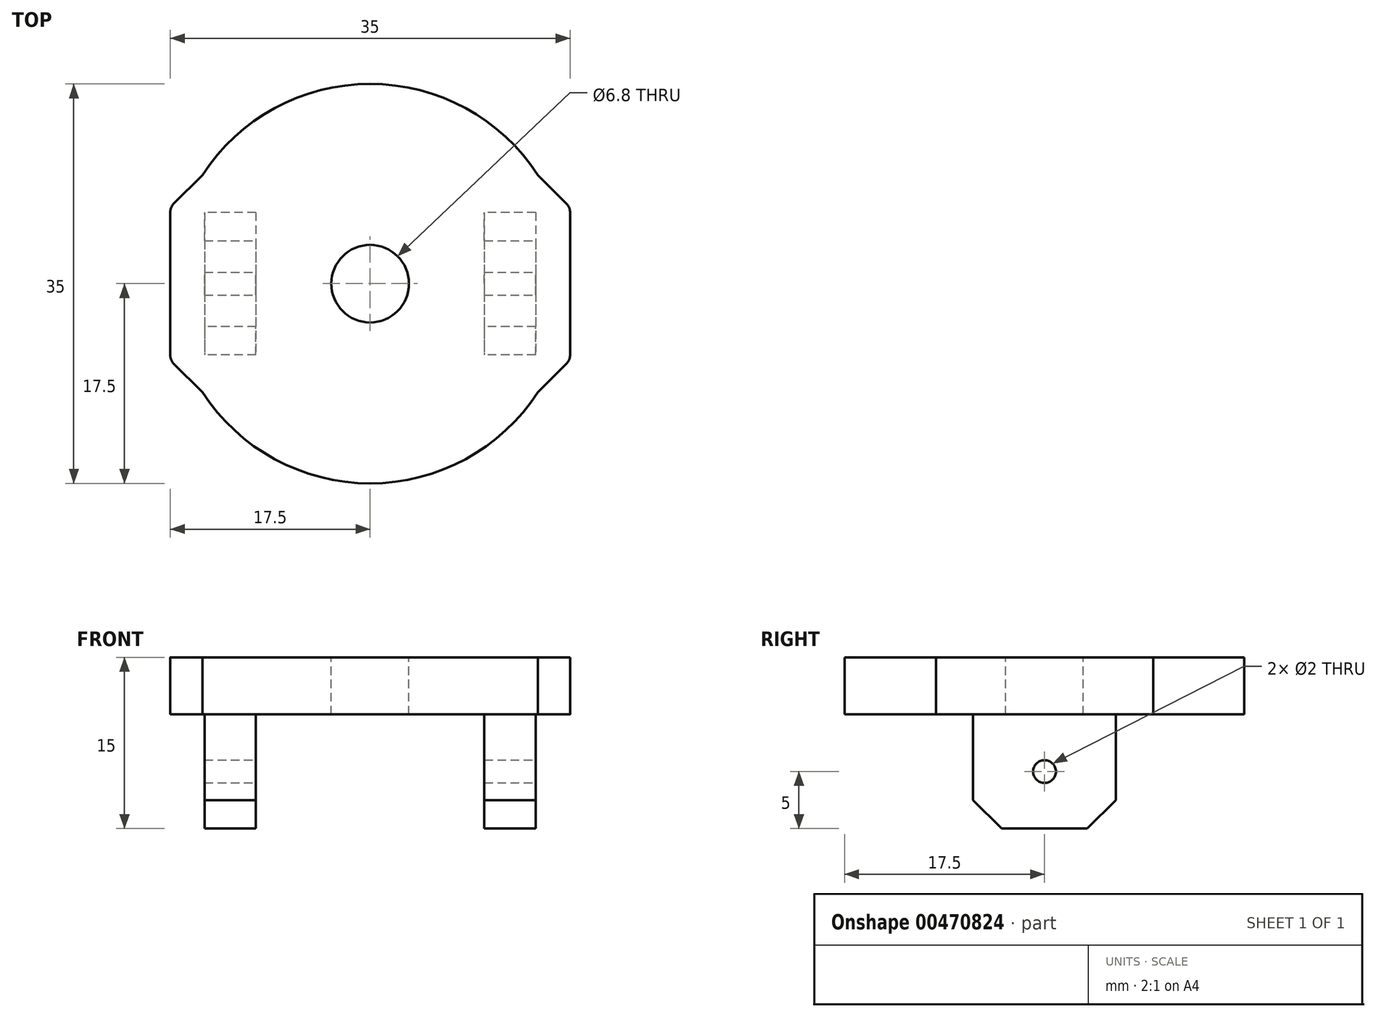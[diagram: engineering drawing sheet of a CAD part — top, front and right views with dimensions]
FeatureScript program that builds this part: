
annotation { "Feature Type Name" : "Feature", "Feature Type Description" : "" }
export const myFeature = defineFeature(function(context is Context, id is Id, definition is map)
    precondition{}
    {
        {
            var Q0;
            Q0=qCreatedBy(makeId("Top.planeOp"),FACE);
            var sketch = newSketch(context, id + "F0", { "sketchPlane" : qUnion([Q0])});
            skLineSegment(sketch, "E0.left", {"start": v(25, -7.7) * mm, "end": v(25, 7.7) * mm});
            skLineSegment(sketch, "E0.right", {"start": v(-25, -7.7) * mm, "end": v(-25, 7.7) * mm});
            skPoint(sketch, "E0.middle", {"position": v(0, 0) * mm});
            skEllipticalArc(sketch, "E1", {});
            skPoint(sketch, "E2.visualSharp", {"position": v(-25, 12.78) * mm});
            skArc(sketch, "E2.filletArc", {"start": v(-19.86, 15.83) * mm, "mid": v(-23.6, 12.5) * mm, "end": v(-25, 7.7) * mm});
            skArc(sketch, "E3.filletArc", {"start": v(-25, -7.7) * mm, "mid": v(-23.6, -12.5) * mm, "end": v(-19.86, -15.83) * mm});
            skEllipticalArc(sketch, "E4.trimOffspring", {});
            skPoint(sketch, "E5.visualSharp", {"position": v(25, 12.78) * mm});
            skArc(sketch, "E5.filletArc", {"start": v(25, 7.7) * mm, "mid": v(23.6, 12.5) * mm, "end": v(19.86, 15.83) * mm});
            skPoint(sketch, "E6.visualSharp", {"position": v(25, -12.78) * mm});
            skArc(sketch, "E6.filletArc", {"start": v(19.86, -15.83) * mm, "mid": v(23.6, -12.5) * mm, "end": v(25, -7.7) * mm});
            const initialGuessF0  = {"E1": [0, 0, 1, 0, 0.0325, 0.02, 4.054867696901255, 5.3699102638681255], "E4.trimOffspring": [0, 0, 1, 0, 0.0325, 0.02, 0.913275043311461, 2.2283176102783337]};
            skSetInitialGuess(sketch, initialGuessF0);
            skSolve(sketch);
        }
        {
            var Q0;
            Q0=makeQuery(id+"F0.imprint","IMPRINT",FACE,{"disambiguationData":[TD([[makeQuery(id+"F0.imprint","IMPRINT",EDGE,{"derivedFrom":sQuery(id+"F0.wireOp",EDGE,"E0.left")}),1.0]])]});
            extrude(context, id + "F1", {"entities" : qUnion([Q0]), "depth" : 5 * mm});
        }
        {
            var Q0;
            Q0=makeQuery(id+"F1.opExtrude","CAP_FACE",FACE,{"disambiguationData":[OSD([sQuery(id+"F0.wireOp",EDGE,"E0.left"),sQuery(id+"F0.wireOp",EDGE,"E0.right"),sQuery(id+"F0.wireOp",EDGE,"E1"),sQuery(id+"F0.wireOp",EDGE,"E2.filletArc"),sQuery(id+"F0.wireOp",EDGE,"E3.filletArc"),sQuery(id+"F0.wireOp",EDGE,"E4.trimOffspring"),sQuery(id+"F0.wireOp",EDGE,"E5.filletArc"),sQuery(id+"F0.wireOp",EDGE,"E6.filletArc")])],"isStart":true});
            var sketch = newSketch(context, id + "F2", { "sketchPlane" : qUnion([Q0])});
            skLineSegment(sketch, "E7.bottom", {"start": v(14.5, -6.25) * mm, "end": v(10, -6.25) * mm});
            skLineSegment(sketch, "E7.top", {"start": v(14.5, 6.25) * mm, "end": v(10, 6.25) * mm});
            skLineSegment(sketch, "E7.left", {"start": v(14.5, -6.25) * mm, "end": v(14.5, 6.25) * mm});
            skLineSegment(sketch, "E7.right", {"start": v(-14.5, -6.25) * mm, "end": v(-14.5, 6.25) * mm});
            skPoint(sketch, "E7.middle", {"position": v(0, 0) * mm});
            skLineSegment(sketch, "E8.left", {"start": v(10, -6.25) * mm, "end": v(10, 6.25) * mm});
            skLineSegment(sketch, "E8.right", {"start": v(-10, -6.25) * mm, "end": v(-10, 6.25) * mm});
            skLineSegment(sketch, "E9.trimOffspring", {"start": v(-10, 6.25) * mm, "end": v(-14.5, 6.25) * mm});
            skLineSegment(sketch, "E10.trimOffspring", {"start": v(-10, -6.25) * mm, "end": v(-14.5, -6.25) * mm});
            skSolve(sketch);
        }
        {
            var Q0;
            Q0=makeQuery(id+"F1.opExtrude","CAP_EDGE",EDGE,{"disambiguationData":[OSD([sQuery(id+"F0.wireOp",EDGE,"E1")])],"isStart":true});
            var Q1;
            Q1=makeQuery(id+"FL3o96M6EoHQmEN_1.opExtrude","CAP_FACE",FACE,{"disambiguationData":[OSD([sQuery(id+"F2.wireOp",EDGE,"E7.bottom"),sQuery(id+"F2.wireOp",EDGE,"E7.top"),sQuery(id+"F2.wireOp",EDGE,"E7.left"),sQuery(id+"F2.wireOp",EDGE,"E7.right")])],"isStart":false});
            chamfer(context, id + "F3", {"entities" : qUnion([Q0, Q1]), "width" : 1 * mm, "tangentPropagation" : true});
        }
        {
            var Q0;
            Q0=qSketchRegion(id+"F2",true);
            extrude(context, id + "F4", {"entities" : qUnion([Q0]), "operationType" : NewBodyOperationType.ADD, "depth" : 10 * mm});
        }
        {
            var Q0;
            Q0=makeQuery(id+"F4.opExtrude","CAP_EDGE",EDGE,{"disambiguationData":[OSD([sQuery(id+"F2.wireOp",EDGE,"E9.trimOffspring")])],"isStart":false});
            var Q1;
            Q1=makeQuery(id+"F4.opExtrude","CAP_EDGE",EDGE,{"disambiguationData":[OSD([sQuery(id+"F2.wireOp",EDGE,"E7.top")])],"isStart":false});
            var Q2;
            Q2=makeQuery(id+"F4.opExtrude","CAP_EDGE",EDGE,{"disambiguationData":[OSD([sQuery(id+"F2.wireOp",EDGE,"E10.trimOffspring")])],"isStart":false});
            var Q3;
            Q3=makeQuery(id+"F4.opExtrude","CAP_EDGE",EDGE,{"disambiguationData":[OSD([sQuery(id+"F2.wireOp",EDGE,"E7.bottom")])],"isStart":false});
            chamfer(context, id + "F5", {"entities" : qUnion([Q0, Q1, Q2, Q3]), "width" : 2.5 * mm, "tangentPropagation" : true});
        }
        {
            var Q0;
            Q0=makeQuery(id+"F4.opExtrude","SWEPT_FACE",FACE,{"disambiguationData":[OSD([sQuery(id+"F2.wireOp",EDGE,"E7.left")])]});
            var sketch = newSketch(context, id + "F6", { "sketchPlane" : qUnion([Q0])});
            skCircle(sketch, "E11", {"center": v(0, -5) * mm, "radius": 1 * mm});
            skSolve(sketch);
        }
        {
            var Q0;
            Q0=qSketchRegion(id+"F6",true);
            extrude(context, id + "F7", {"entities" : qUnion([Q0]), "operationType" : NewBodyOperationType.REMOVE, "endBound" : BoundingType.THROUGH_ALL, "oppositeDirection" : true, "depth" : 25 * mm});
        }
        {
            var Q0;
            Q0=makeQuery(id+"F1.opExtrude","CAP_FACE",FACE,{"disambiguationData":[OSD([sQuery(id+"F0.wireOp",EDGE,"E0.left"),sQuery(id+"F0.wireOp",EDGE,"E0.right"),sQuery(id+"F0.wireOp",EDGE,"E1"),sQuery(id+"F0.wireOp",EDGE,"E2.filletArc"),sQuery(id+"F0.wireOp",EDGE,"E3.filletArc"),sQuery(id+"F0.wireOp",EDGE,"E4.trimOffspring"),sQuery(id+"F0.wireOp",EDGE,"E5.filletArc"),sQuery(id+"F0.wireOp",EDGE,"E6.filletArc")])],"isStart":false});
            var sketch = newSketch(context, id + "F8", { "sketchPlane" : qUnion([Q0])});
            skCircle(sketch, "E12", {"center": v(0, 0) * mm, "radius": 17.5 * mm});
            skCircle(sketch, "E13", {"center": v(0, 0) * mm, "radius": 39.59 * mm});
            skSolve(sketch);
        }
        {
            var Q0;
            Q0=makeQuery(id+"F8.imprint","IMPRINT",FACE,{"disambiguationData":[TD([[makeQuery(id+"F8.imprint","IMPRINT",EDGE,{"derivedFrom":sQuery(id+"F8.wireOp",EDGE,"E12")}),-1.0]])]});
            var Q1;
            Q1=makeQuery(id+"F8.imprint","IMPRINT",FACE,{"disambiguationData":[TD([[makeQuery(id+"F8.imprint","IMPRINT",EDGE,{"derivedFrom":sQuery(id+"F8.wireOp",EDGE,"E13")}),1.0]])]});
            extrude(context, id + "F9", {"entities" : qUnion([Q0, Q1]), "operationType" : NewBodyOperationType.REMOVE, "oppositeDirection" : true, "depth" : 25 * mm});
        }
        {
            var Q0;
            Q0=makeQuery(id+"F1.opExtrude","CAP_FACE",FACE,{"disambiguationData":[OSD([sQuery(id+"F0.wireOp",EDGE,"E0.left"),sQuery(id+"F0.wireOp",EDGE,"E0.right"),sQuery(id+"F0.wireOp",EDGE,"E1"),sQuery(id+"F0.wireOp",EDGE,"E2.filletArc"),sQuery(id+"F0.wireOp",EDGE,"E3.filletArc"),sQuery(id+"F0.wireOp",EDGE,"E4.trimOffspring"),sQuery(id+"F0.wireOp",EDGE,"E5.filletArc"),sQuery(id+"F0.wireOp",EDGE,"E6.filletArc")])],"isStart":false});
            var sketch = newSketch(context, id + "F10", { "sketchPlane" : qUnion([Q0])});
            skCircle(sketch, "E14", {"center": v(0, 0) * mm, "radius": 3.4 * mm});
            skSolve(sketch);
        }
        {
            var Q0;
            Q0=makeQuery(id+"F10.imprint","IMPRINT",FACE,{"disambiguationData":[TD([[makeQuery(id+"F10.imprint","IMPRINT",EDGE,{"derivedFrom":sQuery(id+"F10.wireOp",EDGE,"E14")}),1.0]])]});
            extrude(context, id + "F11", {"entities" : qUnion([Q0]), "operationType" : NewBodyOperationType.REMOVE, "oppositeDirection" : true, "depth" : 25 * mm});
        }
        {
            var Q0;
            Q0=makeQuery(id+"F1.opExtrude","CAP_FACE",FACE,{"disambiguationData":[OSD([sQuery(id+"F0.wireOp",EDGE,"E0.left"),sQuery(id+"F0.wireOp",EDGE,"E0.right"),sQuery(id+"F0.wireOp",EDGE,"E1"),sQuery(id+"F0.wireOp",EDGE,"E2.filletArc"),sQuery(id+"F0.wireOp",EDGE,"E3.filletArc"),sQuery(id+"F0.wireOp",EDGE,"E4.trimOffspring"),sQuery(id+"F0.wireOp",EDGE,"E5.filletArc"),sQuery(id+"F0.wireOp",EDGE,"E6.filletArc")])],"isStart":true});
            var sketch = newSketch(context, id + "F12", { "sketchPlane" : qUnion([Q0])});
            skCircle(sketch, "E15", {"center": v(0, 0) * mm, "radius": 5 * mm});
            skLineSegment(sketch, "E16.bottom", {"start": v(17.5, -12) * mm, "end": v(-17.5, -12) * mm});
            skLineSegment(sketch, "E16.top", {"start": v(17.5, 12) * mm, "end": v(-17.5, 12) * mm});
            skLineSegment(sketch, "E16.left", {"start": v(17.5, -12) * mm, "end": v(17.5, 12) * mm});
            skLineSegment(sketch, "E16.right", {"start": v(-17.5, -12) * mm, "end": v(-17.5, 12) * mm});
            skSolve(sketch);
        }
        {
            var Q0;
            {var subQ0=sQuery(id+"F12.wireOp",EDGE,"E16.right");var subQ1=sQuery(id+"F12.wireOp",EDGE,"E16.top");var subQ2=makeQuery(id+"F12.imprint","INTERSECT",VERTEX,{"derivedFrom":[subQ1,subQ0]});Q0=makeQuery(id+"F12.imprint","IMPRINT",FACE,{"disambiguationData":[TD([[makeQuery(id+"F12.imprint","IMPRINT",EDGE,{"disambiguationData":[TD([[subQ2,1.0]])],"derivedFrom":subQ1}),1.0]])]});}
            var Q1;
            {var subQ0=sQuery(id+"F12.wireOp",EDGE,"E16.left");var subQ1=sQuery(id+"F12.wireOp",EDGE,"E16.top");var subQ2=makeQuery(id+"F12.imprint","INTERSECT",VERTEX,{"derivedFrom":[subQ1,subQ0]});Q1=makeQuery(id+"F12.imprint","IMPRINT",FACE,{"disambiguationData":[TD([[makeQuery(id+"F12.imprint","IMPRINT",EDGE,{"disambiguationData":[TD([[subQ2,-1.0]])],"derivedFrom":subQ1}),1.0]])]});}
            var Q2;
            {var subQ0=sQuery(id+"F12.wireOp",EDGE,"E16.left");var subQ1=sQuery(id+"F12.wireOp",EDGE,"E16.bottom");var subQ2=makeQuery(id+"F12.imprint","INTERSECT",VERTEX,{"derivedFrom":[subQ1,subQ0]});Q2=makeQuery(id+"F12.imprint","IMPRINT",FACE,{"disambiguationData":[TD([[makeQuery(id+"F12.imprint","IMPRINT",EDGE,{"disambiguationData":[TD([[subQ2,-1.0]])],"derivedFrom":subQ1}),-1.0]])]});}
            var Q3;
            {var subQ0=sQuery(id+"F12.wireOp",EDGE,"E16.right");var subQ1=sQuery(id+"F12.wireOp",EDGE,"E16.bottom");var subQ2=makeQuery(id+"F12.imprint","INTERSECT",VERTEX,{"derivedFrom":[subQ1,subQ0]});Q3=makeQuery(id+"F12.imprint","IMPRINT",FACE,{"disambiguationData":[TD([[makeQuery(id+"F12.imprint","IMPRINT",EDGE,{"disambiguationData":[TD([[subQ2,1.0]])],"derivedFrom":subQ1}),-1.0]])]});}
            extrude(context, id + "F13", {"entities" : qUnion([Q0, Q1, Q2, Q3]), "operationType" : NewBodyOperationType.ADD, "oppositeDirection" : true, "depth" : 5 * mm});
        }
        {
            var Q0;
            Q0=makeQuery(id+"F13.opExtrude","SWEPT_EDGE",EDGE,{"disambiguationData":[OSD([sQuery(id+"F12.wireOp",EDGE,"E16.top"),sQuery(id+"F12.wireOp",EDGE,"E16.left")])]});
            var Q1;
            Q1=makeQuery(id+"F13.opExtrude","SWEPT_EDGE",EDGE,{"disambiguationData":[OSD([sQuery(id+"F12.wireOp",EDGE,"E16.bottom"),sQuery(id+"F12.wireOp",EDGE,"E16.left")])]});
            var Q2;
            Q2=makeQuery(id+"F13.opExtrude","SWEPT_EDGE",EDGE,{"disambiguationData":[OSD([sQuery(id+"F12.wireOp",EDGE,"E16.top"),sQuery(id+"F12.wireOp",EDGE,"E16.right")])]});
            var Q3;
            Q3=makeQuery(id+"F13.opExtrude","SWEPT_EDGE",EDGE,{"disambiguationData":[OSD([sQuery(id+"F12.wireOp",EDGE,"E16.bottom"),sQuery(id+"F12.wireOp",EDGE,"E16.right")])]});
            chamfer(context, id + "F14", {"entities" : qUnion([Q0, Q1, Q2, Q3]), "width" : 5.3 * mm, "tangentPropagation" : true});
        }
        {
            var Q0;
            {var subQ0=sQuery(id+"F12.wireOp",EDGE,"E16.right");var subQ1=sQuery(id+"F12.wireOp",EDGE,"E16.top");Q0=makeQuery(id+"F14.opChamfer","BLEND_EDGE",EDGE,{"blendedFrom":[makeQuery(id+"F13.opExtrude","SWEPT_EDGE",EDGE,{"disambiguationData":[OSD([subQ1,subQ0])]}),makeQuery(id+"F13.boolean.opBoolean","MERGE",FACE,{"derivedFrom":[makeQuery(id+"F13.opExtrude","SWEPT_FACE",FACE,{"disambiguationData":[OSD([subQ0]),TDD([makeQuery(id+"F12.imprint","IMPRINT",EDGE,{"disambiguationData":[TD([[makeQuery(id+"F12.imprint","INTERSECT",VERTEX,{"derivedFrom":[sQuery(id+"F12.wireOp",EDGE,"E16.bottom"),subQ0]}),-1.0]])],"derivedFrom":subQ0})])]}),makeQuery(id+"F13.opExtrude","SWEPT_FACE",FACE,{"disambiguationData":[OSD([subQ0]),TDD([makeQuery(id+"F12.imprint","IMPRINT",EDGE,{"disambiguationData":[TD([[makeQuery(id+"F12.imprint","INTERSECT",VERTEX,{"derivedFrom":[subQ1,subQ0]}),1.0]])],"derivedFrom":subQ0})])]})]})],"blendedInto":[makeQuery(id+"F13.boolean.opBoolean","MERGE",FACE,{"derivedFrom":[makeQuery(id+"F13.opExtrude","SWEPT_FACE",FACE,{"disambiguationData":[OSD([subQ0]),TDD([makeQuery(id+"F12.imprint","IMPRINT",EDGE,{"disambiguationData":[TD([[makeQuery(id+"F12.imprint","INTERSECT",VERTEX,{"derivedFrom":[sQuery(id+"F12.wireOp",EDGE,"E16.bottom"),subQ0]}),-1.0]])],"derivedFrom":subQ0})])]}),makeQuery(id+"F13.opExtrude","SWEPT_FACE",FACE,{"disambiguationData":[OSD([subQ0]),TDD([makeQuery(id+"F12.imprint","IMPRINT",EDGE,{"disambiguationData":[TD([[makeQuery(id+"F12.imprint","INTERSECT",VERTEX,{"derivedFrom":[subQ1,subQ0]}),1.0]])],"derivedFrom":subQ0})])]})]})]});}
            var Q1;
            {var subQ0=sQuery(id+"F12.wireOp",EDGE,"E16.right");var subQ2=sQuery(id+"F12.wireOp",EDGE,"E16.bottom");Q1=makeQuery(id+"F14.opChamfer","BLEND_EDGE",EDGE,{"blendedFrom":[makeQuery(id+"F13.opExtrude","SWEPT_EDGE",EDGE,{"disambiguationData":[OSD([subQ2,subQ0])]}),makeQuery(id+"F13.boolean.opBoolean","MERGE",FACE,{"derivedFrom":[makeQuery(id+"F13.opExtrude","SWEPT_FACE",FACE,{"disambiguationData":[OSD([subQ0]),TDD([makeQuery(id+"F12.imprint","IMPRINT",EDGE,{"disambiguationData":[TD([[makeQuery(id+"F12.imprint","INTERSECT",VERTEX,{"derivedFrom":[subQ2,subQ0]}),-1.0]])],"derivedFrom":subQ0})])]}),makeQuery(id+"F13.opExtrude","SWEPT_FACE",FACE,{"disambiguationData":[OSD([subQ0]),TDD([makeQuery(id+"F12.imprint","IMPRINT",EDGE,{"disambiguationData":[TD([[makeQuery(id+"F12.imprint","INTERSECT",VERTEX,{"derivedFrom":[sQuery(id+"F12.wireOp",EDGE,"E16.top"),subQ0]}),1.0]])],"derivedFrom":subQ0})])]})]})],"blendedInto":[makeQuery(id+"F13.boolean.opBoolean","MERGE",FACE,{"derivedFrom":[makeQuery(id+"F13.opExtrude","SWEPT_FACE",FACE,{"disambiguationData":[OSD([subQ0]),TDD([makeQuery(id+"F12.imprint","IMPRINT",EDGE,{"disambiguationData":[TD([[makeQuery(id+"F12.imprint","INTERSECT",VERTEX,{"derivedFrom":[subQ2,subQ0]}),-1.0]])],"derivedFrom":subQ0})])]}),makeQuery(id+"F13.opExtrude","SWEPT_FACE",FACE,{"disambiguationData":[OSD([subQ0]),TDD([makeQuery(id+"F12.imprint","IMPRINT",EDGE,{"disambiguationData":[TD([[makeQuery(id+"F12.imprint","INTERSECT",VERTEX,{"derivedFrom":[sQuery(id+"F12.wireOp",EDGE,"E16.top"),subQ0]}),1.0]])],"derivedFrom":subQ0})])]})]})]});}
            var Q2;
            {var subQ0=sQuery(id+"F12.wireOp",EDGE,"E16.left");var subQ2=sQuery(id+"F12.wireOp",EDGE,"E16.bottom");Q2=makeQuery(id+"F14.opChamfer","BLEND_EDGE",EDGE,{"blendedFrom":[makeQuery(id+"F13.opExtrude","SWEPT_EDGE",EDGE,{"disambiguationData":[OSD([subQ2,subQ0])]}),makeQuery(id+"F13.boolean.opBoolean","MERGE",FACE,{"derivedFrom":[makeQuery(id+"F13.opExtrude","SWEPT_FACE",FACE,{"disambiguationData":[OSD([subQ0]),TDD([makeQuery(id+"F12.imprint","IMPRINT",EDGE,{"disambiguationData":[TD([[makeQuery(id+"F12.imprint","INTERSECT",VERTEX,{"derivedFrom":[subQ2,subQ0]}),-1.0]])],"derivedFrom":subQ0})])]}),makeQuery(id+"F13.opExtrude","SWEPT_FACE",FACE,{"disambiguationData":[OSD([subQ0]),TDD([makeQuery(id+"F12.imprint","IMPRINT",EDGE,{"disambiguationData":[TD([[makeQuery(id+"F12.imprint","INTERSECT",VERTEX,{"derivedFrom":[sQuery(id+"F12.wireOp",EDGE,"E16.top"),subQ0]}),1.0]])],"derivedFrom":subQ0})])]})]})],"blendedInto":[makeQuery(id+"F13.boolean.opBoolean","MERGE",FACE,{"derivedFrom":[makeQuery(id+"F13.opExtrude","SWEPT_FACE",FACE,{"disambiguationData":[OSD([subQ0]),TDD([makeQuery(id+"F12.imprint","IMPRINT",EDGE,{"disambiguationData":[TD([[makeQuery(id+"F12.imprint","INTERSECT",VERTEX,{"derivedFrom":[subQ2,subQ0]}),-1.0]])],"derivedFrom":subQ0})])]}),makeQuery(id+"F13.opExtrude","SWEPT_FACE",FACE,{"disambiguationData":[OSD([subQ0]),TDD([makeQuery(id+"F12.imprint","IMPRINT",EDGE,{"disambiguationData":[TD([[makeQuery(id+"F12.imprint","INTERSECT",VERTEX,{"derivedFrom":[sQuery(id+"F12.wireOp",EDGE,"E16.top"),subQ0]}),1.0]])],"derivedFrom":subQ0})])]})]})]});}
            var Q3;
            {var subQ0=sQuery(id+"F12.wireOp",EDGE,"E16.left");var subQ1=sQuery(id+"F12.wireOp",EDGE,"E16.top");Q3=makeQuery(id+"F14.opChamfer","BLEND_EDGE",EDGE,{"blendedFrom":[makeQuery(id+"F13.opExtrude","SWEPT_EDGE",EDGE,{"disambiguationData":[OSD([subQ1,subQ0])]}),makeQuery(id+"F13.boolean.opBoolean","MERGE",FACE,{"derivedFrom":[makeQuery(id+"F13.opExtrude","SWEPT_FACE",FACE,{"disambiguationData":[OSD([subQ0]),TDD([makeQuery(id+"F12.imprint","IMPRINT",EDGE,{"disambiguationData":[TD([[makeQuery(id+"F12.imprint","INTERSECT",VERTEX,{"derivedFrom":[sQuery(id+"F12.wireOp",EDGE,"E16.bottom"),subQ0]}),-1.0]])],"derivedFrom":subQ0})])]}),makeQuery(id+"F13.opExtrude","SWEPT_FACE",FACE,{"disambiguationData":[OSD([subQ0]),TDD([makeQuery(id+"F12.imprint","IMPRINT",EDGE,{"disambiguationData":[TD([[makeQuery(id+"F12.imprint","INTERSECT",VERTEX,{"derivedFrom":[subQ1,subQ0]}),1.0]])],"derivedFrom":subQ0})])]})]})],"blendedInto":[makeQuery(id+"F13.boolean.opBoolean","MERGE",FACE,{"derivedFrom":[makeQuery(id+"F13.opExtrude","SWEPT_FACE",FACE,{"disambiguationData":[OSD([subQ0]),TDD([makeQuery(id+"F12.imprint","IMPRINT",EDGE,{"disambiguationData":[TD([[makeQuery(id+"F12.imprint","INTERSECT",VERTEX,{"derivedFrom":[sQuery(id+"F12.wireOp",EDGE,"E16.bottom"),subQ0]}),-1.0]])],"derivedFrom":subQ0})])]}),makeQuery(id+"F13.opExtrude","SWEPT_FACE",FACE,{"disambiguationData":[OSD([subQ0]),TDD([makeQuery(id+"F12.imprint","IMPRINT",EDGE,{"disambiguationData":[TD([[makeQuery(id+"F12.imprint","INTERSECT",VERTEX,{"derivedFrom":[subQ1,subQ0]}),1.0]])],"derivedFrom":subQ0})])]})]})]});}
            fillet(context, id + "F15", {"entities" : qUnion([Q0, Q1, Q2, Q3]), "radius" : 1 * mm, "tangentPropagation" : true, "allowEdgeOverflow" : false});
        }
    });
